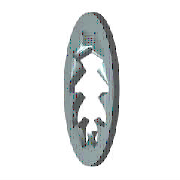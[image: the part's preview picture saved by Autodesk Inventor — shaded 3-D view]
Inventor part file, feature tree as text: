
AUTODESK INVENTOR PART (.ipt)
format: ipt  version: 2021 (Build 250183000, 183)  size: 177,664 bytes
history: native  units: mm (DEFAULTED — no unit token found)
features: sketch x2, extrude x1, pattern_circular x1, other x1, plane x1
ambient origin geometry x7: Origin, YZ Plane, XY Plane, X Axis, Y Axis, Z Axis, Center Point
bodies: Solid1 (feature_tree), Body (feature_tree)
feature tree (6):
  extrude  "Cut"  Depth=10.0mm
  pattern_circular  "Cuts"  [2 undecoded]
  other  "Work Axis2"
  plane  "Work Plane1"
  sketch  "Sketch1"  dims[d0=5.3mm d1=10.0mm]
  sketch  "Sketch2"  dims[d2=0.6mm d3=0.0mm d6=7.65mm d7=1.963495mm d8=0.6mm d9=0.0mm d10=0.159mm d11=80.0mm d13=360.0deg d14=0.0mm d15=0.0mm d20=0.0mm d21=0.0mm]
note: 2 required parameter values undecoded (feature->parameter linkage not recoverable at this tier; creation-order binding heuristic only, values carry confidence <= 0.55)
